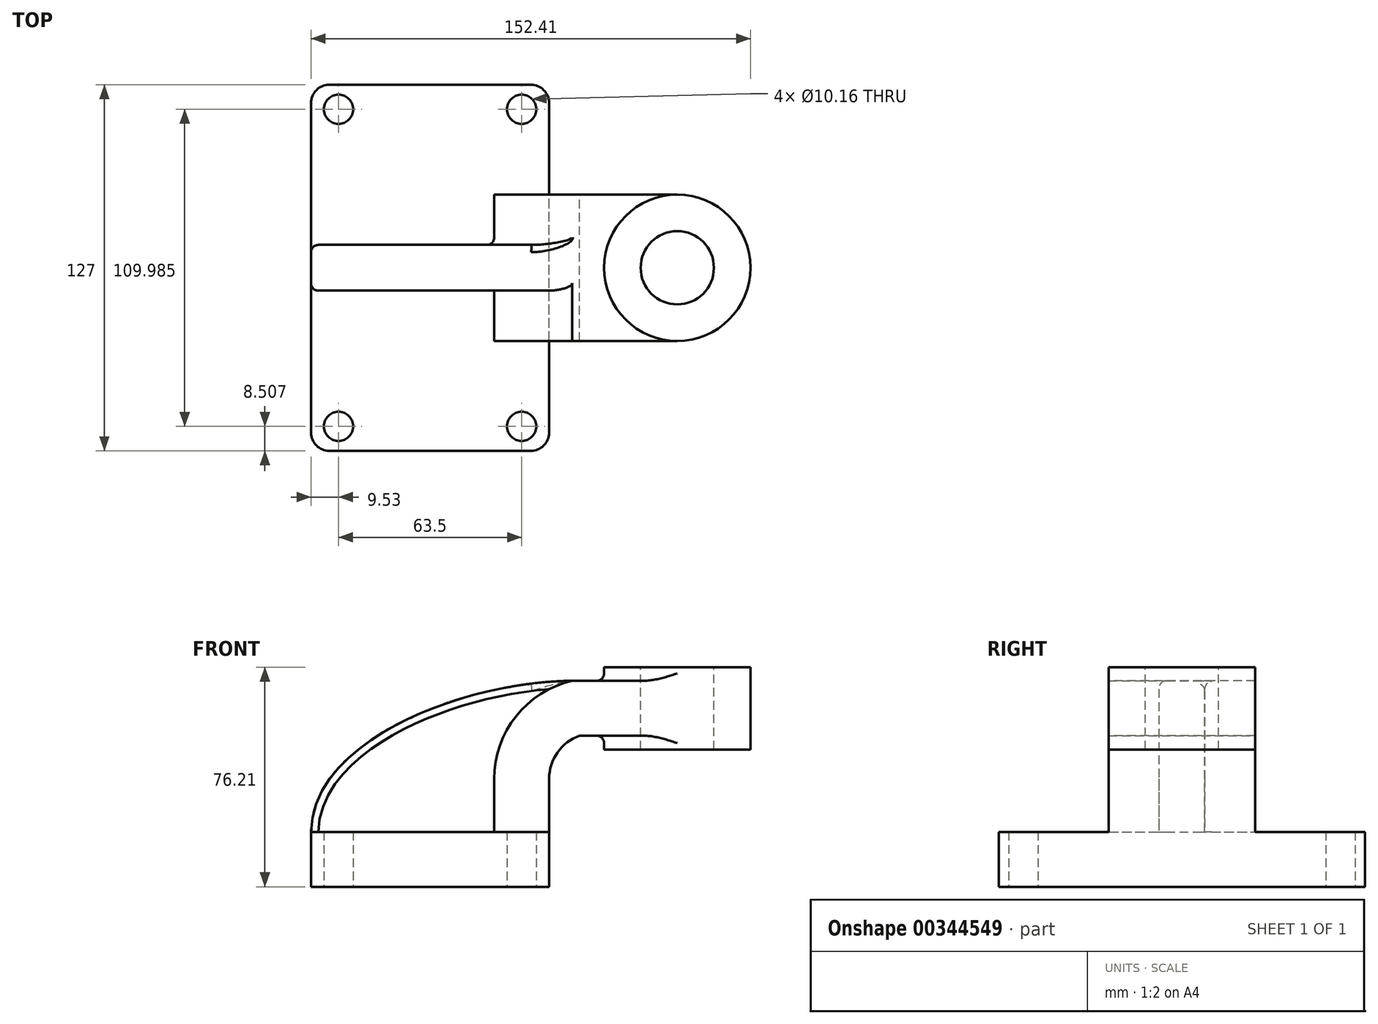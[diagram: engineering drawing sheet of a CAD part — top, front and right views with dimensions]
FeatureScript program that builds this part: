
annotation { "Feature Type Name" : "Feature", "Feature Type Description" : "" }
export const myFeature = defineFeature(function(context is Context, id is Id, definition is map)
    precondition{}
    {
        {
            var Q0;
            Q0=qCreatedBy(makeId("Front.planeOp"),FACE);
            var sketch = newSketch(context, id + "F0", { "sketchPlane" : qUnion([Q0])});
            skLineSegment(sketch, "E0.bottom", {"start": v(41.28, -9.52) * mm, "end": v(-41.28, -9.53) * mm});
            skLineSegment(sketch, "E0.top", {"start": v(41.28, 9.53) * mm, "end": v(-41.28, 9.52) * mm});
            skLineSegment(sketch, "E0.left", {"start": v(41.28, -9.52) * mm, "end": v(41.28, 9.53) * mm});
            skLineSegment(sketch, "E0.right", {"start": v(-41.28, -9.53) * mm, "end": v(-41.28, 9.52) * mm});
            skPoint(sketch, "E0.middle", {"position": v(0, 0) * mm});
            skLineSegment(sketch, "E1.bottom", {"start": v(111.12, 38.1) * mm, "end": v(60.32, 38.1) * mm});
            skLineSegment(sketch, "E1.top", {"start": v(111.12, 66.68) * mm, "end": v(60.32, 66.68) * mm});
            skLineSegment(sketch, "E1.left", {"start": v(111.12, 38.1) * mm, "end": v(111.12, 66.68) * mm});
            skLineSegment(sketch, "E1.right", {"start": v(60.32, 38.1) * mm, "end": v(60.32, 66.68) * mm});
            skPoint(sketch, "E1.middle", {"position": v(85.72, 52.39) * mm});
            skLineSegment(sketch, "E2", {"start": v(41.28, 27.9) * mm, "end": v(41.28, 9.53) * mm});
            skArc(sketch, "E3", {"start": v(41.28, 27.9) * mm, "mid": v(44.19, 37.07) * mm, "end": v(51.85, 42.88) * mm});
            skLineSegment(sketch, "E4", {"start": v(51.85, 42.88) * mm, "end": v(85.72, 42.88) * mm});
            skLineSegment(sketch, "E5.0", {"start": v(22.23, 27.9) * mm, "end": v(22.23, 9.53) * mm});
            skArc(sketch, "E5.1", {"start": v(22.23, 27.9) * mm, "mid": v(29.8, 49.63) * mm, "end": v(49.23, 61.93) * mm});
            skLineSegment(sketch, "E5.2", {"start": v(49.23, 61.93) * mm, "end": v(85.72, 61.93) * mm});
            skLineSegment(sketch, "E6", {"start": v(85.72, 38.1) * mm, "end": v(85.72, 66.68) * mm});
            skFitSpline(sketch, "E7", {"points": [v(-41.28, 9.53) * mm, v(49.23, 61.93) * mm], "startDerivative": vector(1.1, 96.45) * mm, "endDerivative": vector(110.66, 0.95) * mm});
            skSolve(sketch);
        }
        {
            var Q0;
            Q0=makeQuery(id+"F0.imprint","IMPRINT",FACE,{"disambiguationData":[TD([[makeQuery(id+"F0.imprint","IMPRINT",EDGE,{"derivedFrom":sQuery(id+"F0.wireOp",EDGE,"E0.bottom")}),-1.0]])]});
            extrude(context, id + "F1", {"entities" : qUnion([Q0]), "endBound" : BoundingType.SYMMETRIC, "depth" : 127 * mm});
        }
        {
            var Q0;
            {var subQ1=sQuery(id+"F0.wireOp",EDGE,"E2");Q0=makeQuery(id+"F0.imprint","IMPRINT",FACE,{"disambiguationData":[TD([[makeQuery(id+"F0.imprint","IMPRINT",EDGE,{"derivedFrom":subQ1}),-1.0]])]});}
            var Q1;
            {var subQ0=sQuery(id+"F0.wireOp",EDGE,"E4");var subQ1=sQuery(id+"F0.wireOp",EDGE,"E1.right");var subQ2=makeQuery(id+"F0.imprint","INTERSECT",VERTEX,{"derivedFrom":[subQ1,subQ0]});Q1=makeQuery(id+"F0.imprint","IMPRINT",FACE,{"disambiguationData":[TD([[makeQuery(id+"F0.imprint","IMPRINT",EDGE,{"disambiguationData":[TD([[subQ2,-1.0]])],"derivedFrom":subQ1}),-1.0]])]});}
            extrude(context, id + "F2", {"entities" : qUnion([Q0, Q1]), "operationType" : NewBodyOperationType.ADD, "endBound" : BoundingType.SYMMETRIC, "depth" : 50.8 * mm});
        }
        {
            var Q0;
            {var subQ2=sQuery(id+"F0.wireOp",EDGE,"E5.0");Q0=makeQuery(id+"F0.imprint","IMPRINT",FACE,{"disambiguationData":[TD([[makeQuery(id+"F0.imprint","IMPRINT",EDGE,{"derivedFrom":subQ2}),-1.0]])]});}
            extrude(context, id + "F3", {"entities" : qUnion([Q0]), "operationType" : NewBodyOperationType.ADD, "endBound" : BoundingType.SYMMETRIC, "depth" : 15.88 * mm});
        }
        {
            var Q0;
            {var subQ4=sQuery(id+"F0.wireOp",EDGE,"E1.left");Q0=makeQuery(id+"F0.imprint","IMPRINT",FACE,{"disambiguationData":[TD([[makeQuery(id+"F0.imprint","IMPRINT",EDGE,{"derivedFrom":subQ4}),1.0]])]});}
            var Q1;
            Q1=sQuery(id+"F0.wireOp",EDGE,"E6");
            revolve(context, id + "F4", {"operationType" : NewBodyOperationType.ADD, "entities" : qUnion([Q0]), "axis" : qUnion([Q1]), "revolveType" : RevolveType.FULL});
        }
        {
            var Q0;
            Q0=makeQuery(id+"F1.opExtrude","CAP_EDGE",EDGE,{"disambiguationData":[OSD([sQuery(id+"F0.wireOp",EDGE,"E0.right")])],"isStart":false});
            var Q1;
            Q1=makeQuery(id+"F1.opExtrude","CAP_EDGE",EDGE,{"disambiguationData":[OSD([sQuery(id+"F0.wireOp",EDGE,"E0.left")])],"isStart":false});
            fillet(context, id + "F5", {"entities" : qUnion([Q0, Q1]), "radius" : 6.35 * mm, "tangentPropagation" : true, "allowEdgeOverflow" : false});
        }
        {
            var Q0;
            Q0=makeQuery(id+"F1.opExtrude","CAP_EDGE",EDGE,{"disambiguationData":[OSD([sQuery(id+"F0.wireOp",EDGE,"E0.left")])],"isStart":true});
            var Q1;
            Q1=makeQuery(id+"F1.opExtrude","CAP_EDGE",EDGE,{"disambiguationData":[OSD([sQuery(id+"F0.wireOp",EDGE,"E0.right")])],"isStart":true});
            fillet(context, id + "F6", {"entities" : qUnion([Q0, Q1]), "radius" : 6.35 * mm, "tangentPropagation" : true, "allowEdgeOverflow" : false});
        }
        {
            var Q0;
            Q0=qCreatedBy(makeId("Top.planeOp"),FACE);
            var sketch = newSketch(context, id + "F7", { "sketchPlane" : qUnion([Q0])});
            skCircle(sketch, "E8", {"center": v(-31.75, 55) * mm, "radius": 5.08 * mm});
            skCircle(sketch, "E9", {"center": v(31.75, 55) * mm, "radius": 5.08 * mm});
            skCircle(sketch, "E10", {"center": v(-31.75, -55) * mm, "radius": 5.08 * mm});
            skCircle(sketch, "E11", {"center": v(31.75, -55) * mm, "radius": 5.08 * mm});
            skSolve(sketch);
        }
        {
            var Q0;
            Q0=makeQuery(id+"F4.boolean.opBoolean","INTERSECT",EDGE,{"derivedFrom":[makeQuery(id+"F2.opExtrude","SWEPT_FACE",FACE,{"disambiguationData":[OSD([sQuery(id+"F0.wireOp",EDGE,"E5.2")])]}),makeQuery(id+"F4.opRevolve","SWEPT_FACE",FACE,{"disambiguationData":[OSD([sQuery(id+"F0.wireOp",EDGE,"E1.left")])]})]});
            var Q1;
            Q1=makeQuery(id+"F3.opExtrude","CAP_EDGE",EDGE,{"disambiguationData":[OSD([sQuery(id+"F0.wireOp",EDGE,"E5.1")])],"isStart":false});
            var Q2;
            Q2=makeQuery(id+"F3.opExtrude","CAP_EDGE",EDGE,{"disambiguationData":[OSD([sQuery(id+"F0.wireOp",EDGE,"E5.1")])],"isStart":true});
            var Q3;
            Q3=makeQuery(id+"F4.boolean.opBoolean","INTERSECT",EDGE,{"derivedFrom":[makeQuery(id+"F2.opExtrude","SWEPT_FACE",FACE,{"disambiguationData":[OSD([sQuery(id+"F0.wireOp",EDGE,"E4")])]}),makeQuery(id+"F4.opRevolve","SWEPT_FACE",FACE,{"disambiguationData":[OSD([sQuery(id+"F0.wireOp",EDGE,"E1.left")])]})]});
            fillet(context, id + "F8", {"entities" : qUnion([Q0, Q1, Q2, Q3]), "radius" : 2.54 * mm, "tangentPropagation" : true, "allowEdgeOverflow" : false});
        }
        {
            var Q0;
            Q0=sQuery(id+"F7.wireOp",VERTEX,"E10.center");
            var Q1;
            Q1=sQuery(id+"F7.wireOp",VERTEX,"E11.center");
            var Q2;
            Q2=sQuery(id+"F7.wireOp",VERTEX,"E9.center");
            var Q3;
            Q3=sQuery(id+"F7.wireOp",VERTEX,"E8.center");
            var Q4;
            Q4=makeQuery(id+"F1.opExtrude","SWEPT_BODY",BODY,{"disambiguationData":[OSD([sQuery(id+"F0.wireOp",EDGE,"E0.bottom"),sQuery(id+"F0.wireOp",EDGE,"E0.top"),sQuery(id+"F0.wireOp",EDGE,"E0.left"),sQuery(id+"F0.wireOp",EDGE,"E0.right")])]});
            hole(context, id + "F9", {"style" : HoleStyle.SIMPLE, "endStyle" : HoleEndStyle.THROUGH, "oppositeDirection" : true, "holeDiameter" : 10.16 * mm, "tappedDepth" : 12.7 * mm, "tapClearance" : 3, "locations" : qUnion([Q0, Q1, Q2, Q3]), "scope" : qUnion([Q4])});
        }
        {
            var Q0;
            Q0=sQuery(id+"F7.wireOp",VERTEX,"E8.center");
            var Q1;
            Q1=sQuery(id+"F7.wireOp",VERTEX,"E9.center");
            var Q2;
            Q2=sQuery(id+"F7.wireOp",VERTEX,"E11.center");
            var Q3;
            Q3=sQuery(id+"F7.wireOp",VERTEX,"E10.center");
            var Q4;
            Q4=makeQuery(id+"F1.opExtrude","SWEPT_BODY",BODY,{"disambiguationData":[OSD([sQuery(id+"F0.wireOp",EDGE,"E0.bottom"),sQuery(id+"F0.wireOp",EDGE,"E0.top"),sQuery(id+"F0.wireOp",EDGE,"E0.left"),sQuery(id+"F0.wireOp",EDGE,"E0.right")])]});
            hole(context, id + "F10", {"style" : HoleStyle.SIMPLE, "endStyle" : HoleEndStyle.THROUGH, "holeDiameter" : 10.16 * mm, "tappedDepth" : 12.7 * mm, "tapClearance" : 3, "locations" : qUnion([Q0, Q1, Q2, Q3]), "scope" : qUnion([Q4])});
        }
        {
            var Q0;
            Q0=makeQuery(id+"F4.opRevolve","SWEPT_FACE",FACE,{"disambiguationData":[OSD([sQuery(id+"F0.wireOp",EDGE,"E1.top")])]});
            var sketch = newSketch(context, id + "F11", { "sketchPlane" : qUnion([Q0])});
            skCircle(sketch, "E12", {"center": v(85.72, 0) * mm, "radius": 12.7 * mm});
            skSolve(sketch);
        }
        {
            var Q0;
            Q0=sQuery(id+"F11.wireOp",VERTEX,"E12.center");
            var Q1;
            Q1=makeQuery(id+"F1.opExtrude","SWEPT_BODY",BODY,{"disambiguationData":[OSD([sQuery(id+"F0.wireOp",EDGE,"E0.bottom"),sQuery(id+"F0.wireOp",EDGE,"E0.top"),sQuery(id+"F0.wireOp",EDGE,"E0.left"),sQuery(id+"F0.wireOp",EDGE,"E0.right")])]});
            hole(context, id + "F12", {"style" : HoleStyle.SIMPLE, "endStyle" : HoleEndStyle.THROUGH, "holeDiameter" : 25.4 * mm, "tappedDepth" : 12.7 * mm, "tapClearance" : 3, "locations" : qUnion([Q0]), "scope" : qUnion([Q1])});
        }
        {
            var Q0;
            Q0=makeQuery(id+"F3.opExtrude","CAP_EDGE",EDGE,{"disambiguationData":[OSD([sQuery(id+"F0.wireOp",EDGE,"E7")])],"isStart":false});
            var Q1;
            Q1=makeQuery(id+"F3.opExtrude","CAP_EDGE",EDGE,{"disambiguationData":[OSD([sQuery(id+"F0.wireOp",EDGE,"E7")])],"isStart":true});
            fillet(context, id + "F13", {"entities" : qUnion([Q0, Q1]), "radius" : 2.54 * mm, "tangentPropagation" : true, "allowEdgeOverflow" : false});
        }
    });
